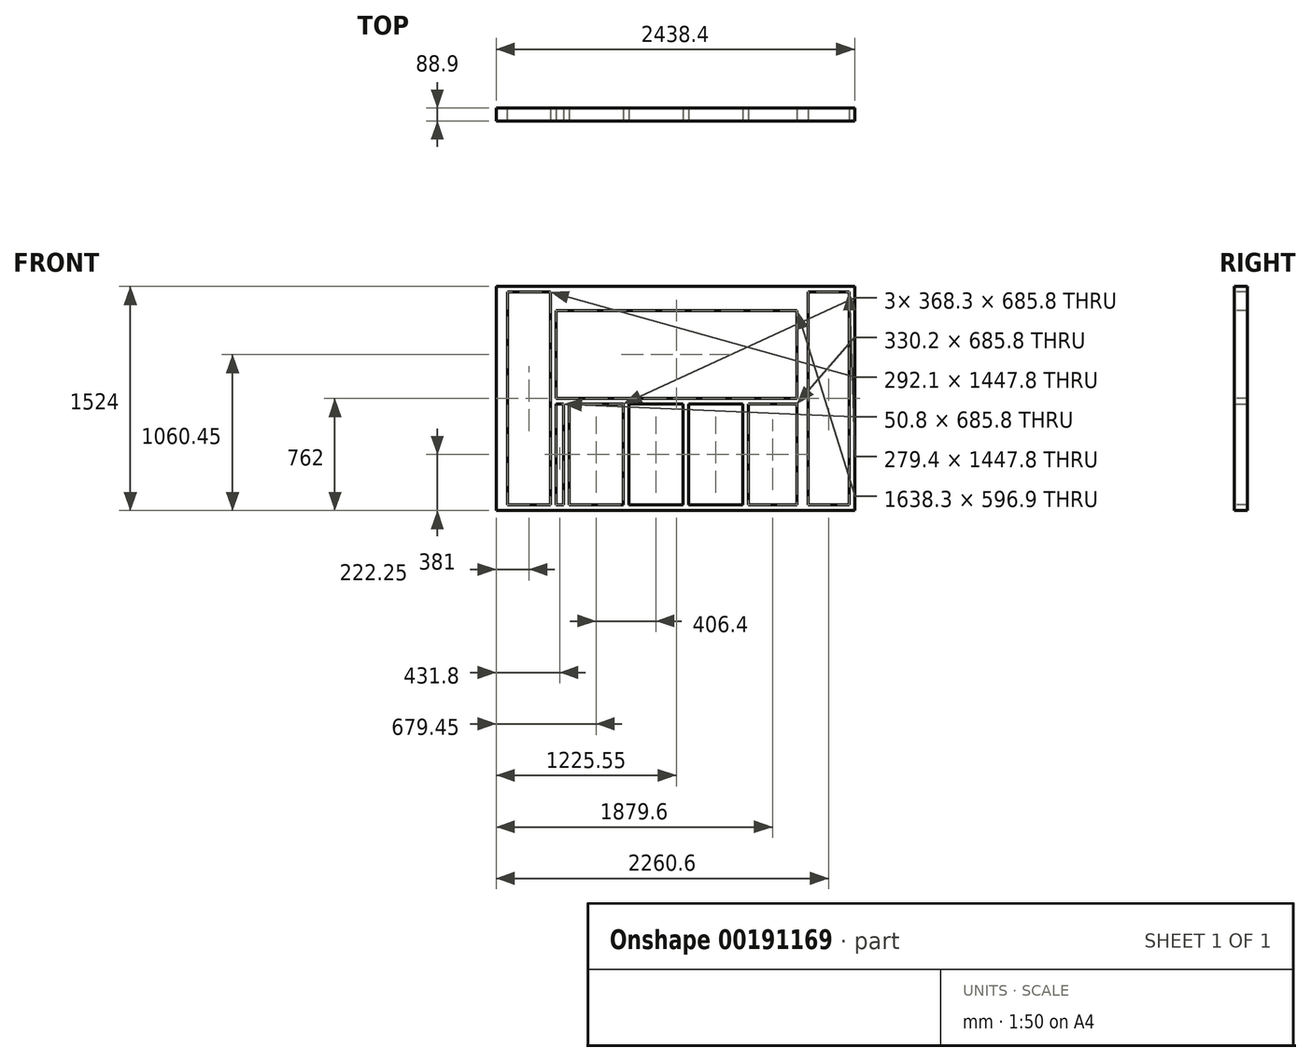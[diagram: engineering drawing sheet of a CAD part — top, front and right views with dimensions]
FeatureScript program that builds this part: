
annotation { "Feature Type Name" : "Feature", "Feature Type Description" : "" }
export const myFeature = defineFeature(function(context is Context, id is Id, definition is map)
    precondition{}
    {
        {
            var Q0;
            Q0=qCreatedBy(makeId("Top.planeOp"),FACE);
            var sketch = newSketch(context, id + "F0", { "sketchPlane" : qUnion([Q0])});
            skLineSegment(sketch, "E0.bottom", {"start": v(1219.2, -44.45) * mm, "end": v(-1219.2, -44.45) * mm});
            skLineSegment(sketch, "E0.top", {"start": v(1219.2, 44.45) * mm, "end": v(-1219.2, 44.45) * mm});
            skLineSegment(sketch, "E0.left", {"start": v(1219.2, -44.45) * mm, "end": v(1219.2, 44.45) * mm});
            skLineSegment(sketch, "E0.right", {"start": v(-1219.2, -44.45) * mm, "end": v(-1219.2, 44.45) * mm});
            skPoint(sketch, "E0.middle", {"position": v(0, 0) * mm});
            skSolve(sketch);
        }
        {
            var Q0;
            Q0 = qSketchRegion(id + "F0", true);
            extrude(context, id + "F1", {"entities" : qUnion([Q0]), "depth" : 38.1 * mm});
        }
        {
            var Q0;
            Q0=makeQuery(id+"F1.opExtrude","CAP_FACE",FACE,{"disambiguationData":[OSD([sQuery(id+"F0.wireOp",EDGE,"E0.bottom"),sQuery(id+"F0.wireOp",EDGE,"E0.top"),sQuery(id+"F0.wireOp",EDGE,"E0.left"),sQuery(id+"F0.wireOp",EDGE,"E0.right")])],"isStart":false});
            var sketch = newSketch(context, id + "F2", { "sketchPlane" : qUnion([Q0])});
            skLineSegment(sketch, "E1.bottom", {"start": v(1219.2, 44.45) * mm, "end": v(1181.1, 44.45) * mm});
            skLineSegment(sketch, "E1.top", {"start": v(1219.2, -44.45) * mm, "end": v(1181.1, -44.45) * mm});
            skLineSegment(sketch, "E1.left", {"start": v(1219.2, 44.45) * mm, "end": v(1219.2, -44.45) * mm});
            skLineSegment(sketch, "E1.right", {"start": v(1181.1, 44.45) * mm, "end": v(1181.1, -44.45) * mm});
            skLineSegment(sketch, "E2.bottom", {"start": v(901.7, 44.45) * mm, "end": v(863.6, 44.45) * mm});
            skLineSegment(sketch, "E2.top", {"start": v(901.7, -44.45) * mm, "end": v(863.6, -44.45) * mm});
            skLineSegment(sketch, "E2.left", {"start": v(901.7, 44.45) * mm, "end": v(901.7, -44.45) * mm});
            skLineSegment(sketch, "E2.right", {"start": v(863.6, 44.45) * mm, "end": v(863.6, -44.45) * mm});
            skLineSegment(sketch, "E3.bottom", {"start": v(495.3, 44.45) * mm, "end": v(457.2, 44.45) * mm});
            skLineSegment(sketch, "E3.top", {"start": v(495.3, -44.45) * mm, "end": v(457.2, -44.45) * mm});
            skLineSegment(sketch, "E3.left", {"start": v(495.3, 44.45) * mm, "end": v(495.3, -44.45) * mm});
            skLineSegment(sketch, "E3.right", {"start": v(457.2, 44.45) * mm, "end": v(457.2, -44.45) * mm});
            skLineSegment(sketch, "E4.bottom", {"start": v(88.9, 44.45) * mm, "end": v(50.8, 44.45) * mm});
            skLineSegment(sketch, "E4.top", {"start": v(88.9, -44.45) * mm, "end": v(50.8, -44.45) * mm});
            skLineSegment(sketch, "E4.left", {"start": v(88.9, 44.45) * mm, "end": v(88.9, -44.45) * mm});
            skLineSegment(sketch, "E4.right", {"start": v(50.8, 44.45) * mm, "end": v(50.8, -44.45) * mm});
            skLineSegment(sketch, "E5.bottom", {"start": v(-317.5, 44.45) * mm, "end": v(-355.6, 44.45) * mm});
            skLineSegment(sketch, "E5.top", {"start": v(-317.5, -44.45) * mm, "end": v(-355.6, -44.45) * mm});
            skLineSegment(sketch, "E5.left", {"start": v(-317.5, 44.45) * mm, "end": v(-317.5, -44.45) * mm});
            skLineSegment(sketch, "E5.right", {"start": v(-355.6, 44.45) * mm, "end": v(-355.6, -44.45) * mm});
            skLineSegment(sketch, "E6.bottom", {"start": v(-723.9, 44.45) * mm, "end": v(-762, 44.45) * mm});
            skLineSegment(sketch, "E6.top", {"start": v(-723.9, -44.45) * mm, "end": v(-762, -44.45) * mm});
            skLineSegment(sketch, "E6.left", {"start": v(-723.9, 44.45) * mm, "end": v(-723.9, -44.45) * mm});
            skLineSegment(sketch, "E6.right", {"start": v(-762, 44.45) * mm, "end": v(-762, -44.45) * mm});
            skLineSegment(sketch, "E7.bottom", {"start": v(-1219.2, -44.45) * mm, "end": v(-1181.1, -44.45) * mm});
            skLineSegment(sketch, "E7.top", {"start": v(-1219.2, 44.45) * mm, "end": v(-1181.1, 44.45) * mm});
            skLineSegment(sketch, "E7.left", {"start": v(-1219.2, -44.45) * mm, "end": v(-1219.2, 44.45) * mm});
            skLineSegment(sketch, "E7.right", {"start": v(-1181.1, -44.45) * mm, "end": v(-1181.1, 44.45) * mm});
            skLineSegment(sketch, "E8.bottom", {"start": v(-1181.1, -44.45) * mm, "end": v(-1143, -44.45) * mm});
            skLineSegment(sketch, "E8.top", {"start": v(-1181.1, 44.45) * mm, "end": v(-1143, 44.45) * mm});
            skLineSegment(sketch, "E8.right", {"start": v(-1143, -44.45) * mm, "end": v(-1143, 44.45) * mm});
            skSolve(sketch);
        }
        {
            var Q0;
            Q0 = qSketchRegion(id + "F2", true);
            extrude(context, id + "F3", {"entities" : qUnion([Q0]), "operationType" : NewBodyOperationType.ADD, "depth" : 1447.8 * mm});
        }
        {
            var Q0;
            Q0=makeQuery(id+"F3.boolean.opBoolean","MERGE",FACE,{"derivedFrom":[makeQuery(id+"F1.opExtrude","SWEPT_FACE",FACE,{"disambiguationData":[OSD([sQuery(id+"F0.wireOp",EDGE,"E0.top")])]}),makeQuery(id+"F3.opExtrude","SWEPT_FACE",FACE,{"disambiguationData":[OSD([sQuery(id+"F2.wireOp",EDGE,"E1.bottom")])]}),makeQuery(id+"F3.opExtrude","SWEPT_FACE",FACE,{"disambiguationData":[OSD([sQuery(id+"F2.wireOp",EDGE,"E2.bottom")])]}),makeQuery(id+"F3.opExtrude","SWEPT_FACE",FACE,{"disambiguationData":[OSD([sQuery(id+"F2.wireOp",EDGE,"E3.bottom")])]}),makeQuery(id+"F3.opExtrude","SWEPT_FACE",FACE,{"disambiguationData":[OSD([sQuery(id+"F2.wireOp",EDGE,"E4.bottom")])]}),makeQuery(id+"F3.opExtrude","SWEPT_FACE",FACE,{"disambiguationData":[OSD([sQuery(id+"F2.wireOp",EDGE,"E5.bottom")])]}),makeQuery(id+"F3.opExtrude","SWEPT_FACE",FACE,{"disambiguationData":[OSD([sQuery(id+"F2.wireOp",EDGE,"E6.bottom")])]}),makeQuery(id+"F3.opExtrude","SWEPT_FACE",FACE,{"disambiguationData":[OSD([sQuery(id+"F2.wireOp",EDGE,"E7.top"),sQuery(id+"F2.wireOp",EDGE,"E8.top")])]})]});
            var sketch = newSketch(context, id + "F4", { "sketchPlane" : qUnion([Q0])});
            skLineSegment(sketch, "E9.bottom", {"start": v(1219.2, 1485.9) * mm, "end": v(-1219.2, 1485.9) * mm});
            skLineSegment(sketch, "E9.top", {"start": v(1219.2, 1524) * mm, "end": v(-1219.2, 1524) * mm});
            skLineSegment(sketch, "E9.left", {"start": v(1219.2, 1485.9) * mm, "end": v(1219.2, 1524) * mm});
            skLineSegment(sketch, "E9.right", {"start": v(-1219.2, 1485.9) * mm, "end": v(-1219.2, 1524) * mm});
            skSolve(sketch);
        }
        {
            var Q0;
            Q0 = qSketchRegion(id + "F4", true);
            extrude(context, id + "F5", {"entities" : qUnion([Q0]), "operationType" : NewBodyOperationType.ADD, "oppositeDirection" : true, "depth" : 88.9 * mm});
        }
        {
            var Q0;
            Q0=makeQuery(id+"F5.boolean.opBoolean","MERGE",FACE,{"derivedFrom":[makeQuery(id+"F3.boolean.opBoolean","MERGE",FACE,{"derivedFrom":[makeQuery(id+"F1.opExtrude","SWEPT_FACE",FACE,{"disambiguationData":[OSD([sQuery(id+"F0.wireOp",EDGE,"E0.bottom")])]}),makeQuery(id+"F3.opExtrude","SWEPT_FACE",FACE,{"disambiguationData":[OSD([sQuery(id+"F2.wireOp",EDGE,"E1.top")])]}),makeQuery(id+"F3.opExtrude","SWEPT_FACE",FACE,{"disambiguationData":[OSD([sQuery(id+"F2.wireOp",EDGE,"E2.top")])]}),makeQuery(id+"F3.opExtrude","SWEPT_FACE",FACE,{"disambiguationData":[OSD([sQuery(id+"F2.wireOp",EDGE,"E3.top")])]}),makeQuery(id+"F3.opExtrude","SWEPT_FACE",FACE,{"disambiguationData":[OSD([sQuery(id+"F2.wireOp",EDGE,"E4.top")])]}),makeQuery(id+"F3.opExtrude","SWEPT_FACE",FACE,{"disambiguationData":[OSD([sQuery(id+"F2.wireOp",EDGE,"E5.top")])]}),makeQuery(id+"F3.opExtrude","SWEPT_FACE",FACE,{"disambiguationData":[OSD([sQuery(id+"F2.wireOp",EDGE,"E6.top")])]}),makeQuery(id+"F3.opExtrude","SWEPT_FACE",FACE,{"disambiguationData":[OSD([sQuery(id+"F2.wireOp",EDGE,"E7.bottom"),sQuery(id+"F2.wireOp",EDGE,"E8.bottom")])]})]}),makeQuery(id+"F5.opExtrude","CAP_FACE",FACE,{"disambiguationData":[OSD([sQuery(id+"F4.wireOp",EDGE,"E9.bottom"),sQuery(id+"F4.wireOp",EDGE,"E9.top"),sQuery(id+"F4.wireOp",EDGE,"E9.left"),sQuery(id+"F4.wireOp",EDGE,"E9.right")])],"isStart":false})]});
            var sketch = newSketch(context, id + "F6", { "sketchPlane" : qUnion([Q0])});
            skLineSegment(sketch, "E10.bottom", {"start": v(812.8, 762) * mm, "end": v(-812.8, 762) * mm});
            skLineSegment(sketch, "E10.top", {"start": v(812.8, 1358.9) * mm, "end": v(-812.8, 1358.9) * mm});
            skLineSegment(sketch, "E10.left", {"start": v(812.8, 762) * mm, "end": v(812.8, 1358.9) * mm});
            skLineSegment(sketch, "E10.right", {"start": v(-812.8, 762) * mm, "end": v(-812.8, 1358.9) * mm});
            skPoint(sketch, "E10.middle", {"position": v(0, 1060.45) * mm});
            skPoint(sketch, "E10.cornerSnap0", {"position": v(-317.5, 762) * mm});
            skLineSegment(sketch, "E11.bottom", {"start": v(-812.8, 1485.9) * mm, "end": v(-850.9, 1485.9) * mm});
            skLineSegment(sketch, "E11.top", {"start": v(-812.8, 38.1) * mm, "end": v(-850.9, 38.1) * mm});
            skLineSegment(sketch, "E11.left", {"start": v(-812.8, 1485.9) * mm, "end": v(-812.8, 38.1) * mm});
            skLineSegment(sketch, "E11.right", {"start": v(-850.9, 1485.9) * mm, "end": v(-850.9, 38.1) * mm});
            skLineSegment(sketch, "E12.bottom", {"start": v(863.6, 38.1) * mm, "end": v(825.5, 38.1) * mm});
            skLineSegment(sketch, "E12.top", {"start": v(863.6, 1485.9) * mm, "end": v(825.5, 1485.9) * mm});
            skLineSegment(sketch, "E12.left", {"start": v(863.6, 38.1) * mm, "end": v(863.6, 1485.9) * mm});
            skLineSegment(sketch, "E12.right", {"start": v(825.5, 38.1) * mm, "end": v(825.5, 1485.9) * mm});
            skLineSegment(sketch, "E13.bottom", {"start": v(-812.8, 762) * mm, "end": v(825.5, 762) * mm});
            skLineSegment(sketch, "E13.top", {"start": v(-812.8, 723.9) * mm, "end": v(825.5, 723.9) * mm});
            skLineSegment(sketch, "E13.left", {"start": v(-812.8, 762) * mm, "end": v(-812.8, 723.9) * mm});
            skLineSegment(sketch, "E13.right", {"start": v(825.5, 762) * mm, "end": v(825.5, 723.9) * mm});
            skLineSegment(sketch, "E14.bottom", {"start": v(-812.8, 1358.9) * mm, "end": v(825.5, 1358.9) * mm});
            skLineSegment(sketch, "E14.top", {"start": v(-812.8, 1485.9) * mm, "end": v(825.5, 1485.9) * mm});
            skLineSegment(sketch, "E14.left", {"start": v(-812.8, 1358.9) * mm, "end": v(-812.8, 1485.9) * mm});
            skLineSegment(sketch, "E14.right", {"start": v(825.5, 1358.9) * mm, "end": v(825.5, 1485.9) * mm});
            skSolve(sketch);
        }
        {
            var Q0;
            Q0 = qSketchRegion(id + "F6", true);
            extrude(context, id + "F7", {"entities" : qUnion([Q0]), "operationType" : NewBodyOperationType.ADD, "oppositeDirection" : true, "depth" : 88.9 * mm});
        }
        {
            var Q0;
            Q0=makeQuery(id+"F7.boolean.opBoolean","MERGE",FACE,{"derivedFrom":[makeQuery(id+"F5.boolean.opBoolean","MERGE",FACE,{"derivedFrom":[makeQuery(id+"F3.boolean.opBoolean","MERGE",FACE,{"derivedFrom":[makeQuery(id+"F1.opExtrude","SWEPT_FACE",FACE,{"disambiguationData":[OSD([sQuery(id+"F0.wireOp",EDGE,"E0.bottom")])]}),makeQuery(id+"F3.opExtrude","SWEPT_FACE",FACE,{"disambiguationData":[OSD([sQuery(id+"F2.wireOp",EDGE,"E1.top")])]}),makeQuery(id+"F3.opExtrude","SWEPT_FACE",FACE,{"disambiguationData":[OSD([sQuery(id+"F2.wireOp",EDGE,"E2.top")])]}),makeQuery(id+"F3.opExtrude","SWEPT_FACE",FACE,{"disambiguationData":[OSD([sQuery(id+"F2.wireOp",EDGE,"E3.top")])]}),makeQuery(id+"F3.opExtrude","SWEPT_FACE",FACE,{"disambiguationData":[OSD([sQuery(id+"F2.wireOp",EDGE,"E4.top")])]}),makeQuery(id+"F3.opExtrude","SWEPT_FACE",FACE,{"disambiguationData":[OSD([sQuery(id+"F2.wireOp",EDGE,"E5.top")])]}),makeQuery(id+"F3.opExtrude","SWEPT_FACE",FACE,{"disambiguationData":[OSD([sQuery(id+"F2.wireOp",EDGE,"E6.top")])]}),makeQuery(id+"F3.opExtrude","SWEPT_FACE",FACE,{"disambiguationData":[OSD([sQuery(id+"F2.wireOp",EDGE,"E7.bottom"),sQuery(id+"F2.wireOp",EDGE,"E8.bottom")])]})]}),makeQuery(id+"F5.opExtrude","CAP_FACE",FACE,{"disambiguationData":[OSD([sQuery(id+"F4.wireOp",EDGE,"E9.bottom"),sQuery(id+"F4.wireOp",EDGE,"E9.top"),sQuery(id+"F4.wireOp",EDGE,"E9.left"),sQuery(id+"F4.wireOp",EDGE,"E9.right")])],"isStart":false})]}),makeQuery(id+"F7.opExtrude","CAP_FACE",FACE,{"disambiguationData":[OSD([sQuery(id+"F6.wireOp",EDGE,"E11.bottom"),sQuery(id+"F6.wireOp",EDGE,"E11.top"),sQuery(id+"F6.wireOp",EDGE,"E11.left"),sQuery(id+"F6.wireOp",EDGE,"E11.right"),sQuery(id+"F6.wireOp",EDGE,"E12.bottom"),sQuery(id+"F6.wireOp",EDGE,"E12.top"),sQuery(id+"F6.wireOp",EDGE,"E12.left"),sQuery(id+"F6.wireOp",EDGE,"E12.right"),sQuery(id+"F6.wireOp",EDGE,"E13.bottom"),sQuery(id+"F6.wireOp",EDGE,"E13.top"),sQuery(id+"F6.wireOp",EDGE,"E14.bottom"),sQuery(id+"F6.wireOp",EDGE,"E14.top")])],"isStart":true})]});
            var sketch = newSketch(context, id + "F8", { "sketchPlane" : qUnion([Q0])});
            skLineSegment(sketch, "E15.bottom", {"start": v(-812.8, 1358.9) * mm, "end": v(825.5, 1358.9) * mm});
            skLineSegment(sketch, "E15.top", {"start": v(-812.8, 762) * mm, "end": v(825.5, 762) * mm});
            skLineSegment(sketch, "E15.left", {"start": v(-812.8, 1358.9) * mm, "end": v(-812.8, 762) * mm});
            skLineSegment(sketch, "E15.right", {"start": v(825.5, 1358.9) * mm, "end": v(825.5, 762) * mm});
            skSolve(sketch);
        }
        {
            var Q0;
            Q0 = qSketchRegion(id + "F8", true);
            extrude(context, id + "F9", {"entities" : qUnion([Q0]), "operationType" : NewBodyOperationType.REMOVE, "oppositeDirection" : true, "depth" : 215.9 * mm});
        }
    });
